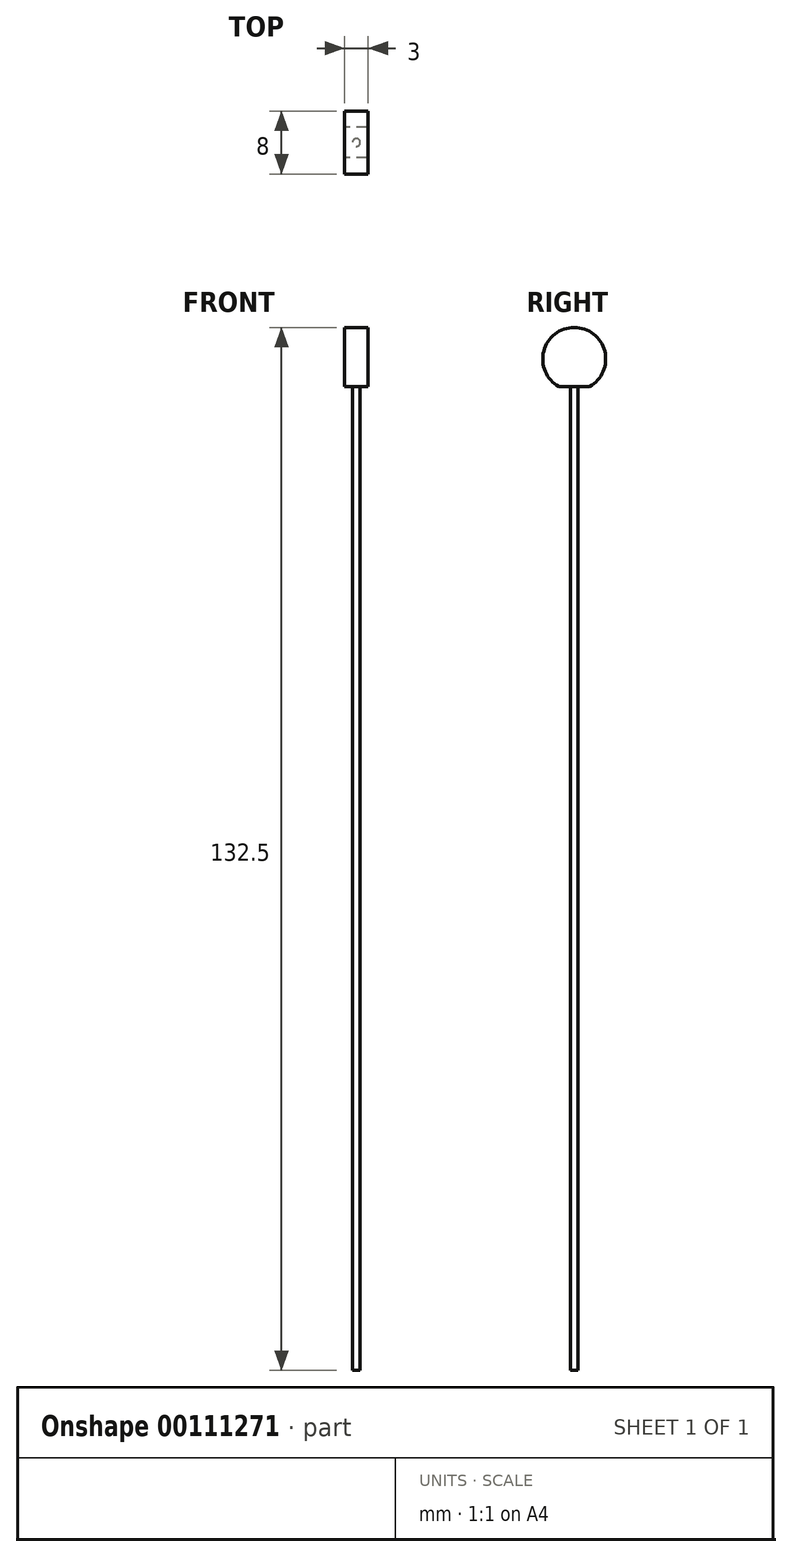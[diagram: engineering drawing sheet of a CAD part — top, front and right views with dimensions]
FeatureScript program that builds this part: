
annotation { "Feature Type Name" : "Feature", "Feature Type Description" : "" }
export const myFeature = defineFeature(function(context is Context, id is Id, definition is map)
    precondition{}
    {
        {
            var Q0;
            Q0=qCreatedBy(makeId("Top.planeOp"),FACE);
            var sketch = newSketch(context, id + "F0", { "sketchPlane" : qUnion([Q0])});
            skCircle(sketch, "E0", {"center": v(0, 0) * mm, "radius": 0.5 * mm});
            skSolve(sketch);
        }
        {
            var Q0;
            Q0=makeQuery(id+"F0.imprint","IMPRINT",FACE,{"disambiguationData":[TD([[makeQuery(id+"F0.imprint","IMPRINT",EDGE,{"derivedFrom":sQuery(id+"F0.wireOp",EDGE,"E0")}),1.0]])]});
            extrude(context, id + "F1", {"entities" : qUnion([Q0]), "endBound" : BoundingType.SYMMETRIC, "depth" : 125 * mm});
        }
        {
            var Q0;
            Q0=qCreatedBy(makeId("Right.planeOp"),FACE);
            var sketch = newSketch(context, id + "F2", { "sketchPlane" : qUnion([Q0])});
            skCircle(sketch, "E1", {"center": v(0, 66) * mm, "radius": 4 * mm});
            skLineSegment(sketch, "E2", {"start": v(-1.94, 62.5) * mm, "end": v(1.94, 62.5) * mm});
            skSolve(sketch);
        }
        {
            var Q0;
            {var subQ0=sQuery(id+"F2.wireOp",EDGE,"E2");Q0=makeQuery(id+"F2.imprint","IMPRINT",FACE,{"disambiguationData":[TD([[makeQuery(id+"F2.imprint","IMPRINT",EDGE,{"derivedFrom":subQ0}),1.0]])]});}
            extrude(context, id + "F3", {"entities" : qUnion([Q0]), "operationType" : NewBodyOperationType.ADD, "endBound" : BoundingType.SYMMETRIC, "depth" : 3 * mm});
        }
    });
